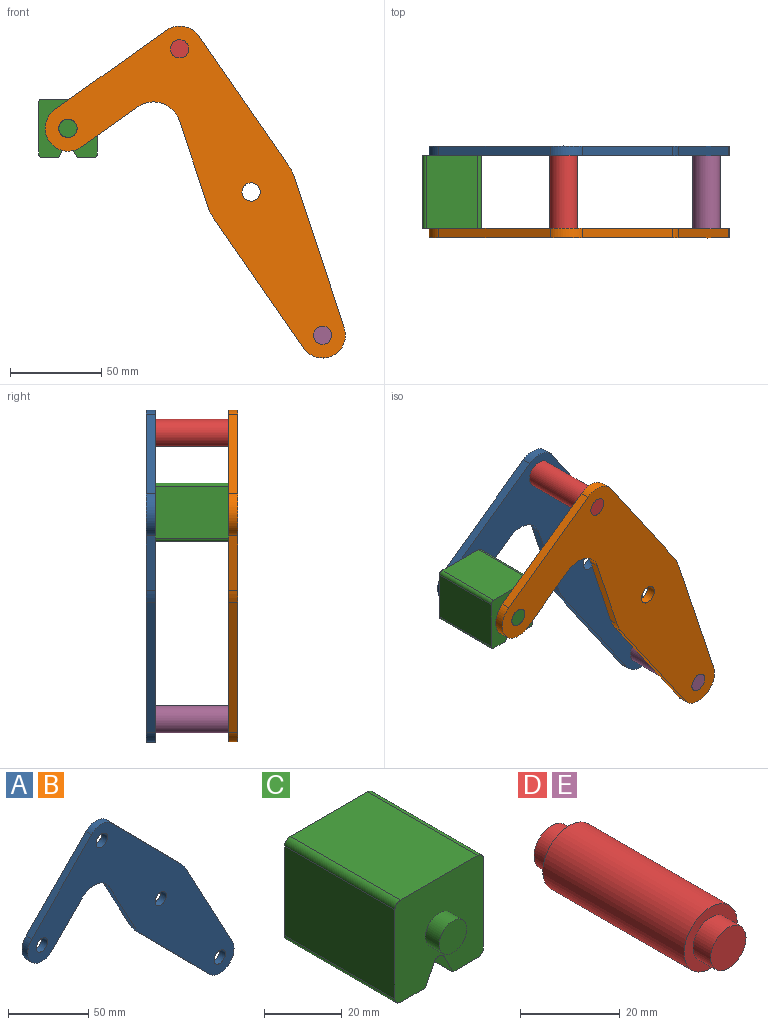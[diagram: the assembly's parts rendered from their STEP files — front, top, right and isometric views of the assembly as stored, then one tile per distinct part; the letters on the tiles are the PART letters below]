
ASSEMBLY  parts=5 mates=3
PART A: 18 faces, bbox 181.7x5x165.8 mm
  f0: plane 43.49x23.35mm, normal (-0.88,0,-0.47), area 246.8mm2, adj f1,f14,f16,f17
  f1: cylinder r=25mm len=5.75mm, axis (0,1,0), area 35.8mm2, adj f0,f2,f16,f17
  f2: plane 61.6x60.87mm, normal (-0.71,0,-0.7), area 433mm2, adj f1,f3,f16,f17
  f3: cylinder r=12.5mm len=21.39mm, axis (0,1,0), area 178.4mm2, adj f2,f4,f16,f17
  f4: plane 76.3x40.96mm, normal (0.88,0,0.47), area 433mm2, adj f3,f5,f16,f17
  f5: cylinder r=25mm len=5.75mm, axis (0,1,0), area 35.8mm2, adj f4,f6,f16,f17
  f6: plane 61.6x60.87mm, normal (0.71,0,0.7), area 433mm2, adj f5,f7,f16,f17
  f7: cylinder r=12.5mm len=17.78mm, axis (0,1,0), area 98.9mm2, adj f6,f8,f16,f17
  f8: plane 53.35x52.71mm, normal (-0.71,0,0.7), area 375mm2, adj f7,f9,f16,f17
  f9: cylinder r=12.5mm len=21.39mm, axis (0,1,0), area 196.3mm2, adj f8,f10,f16,f17
  f10: plane 26.86x26.54mm, normal (0.71,0,-0.7), area 188.8mm2, adj f9,f14,f16,f17
  f11: cylinder r=5mm len=10mm, axis (0,1,0), area 157.1mm2, adj f16,f17
  f12: cylinder r=5mm len=10mm, axis (0,1,0), area 157.1mm2, adj f16,f17
  f13: cylinder r=5mm len=10mm, axis (0,1,0), area 157.1mm2, adj f16,f17
  f14: cylinder r=15mm len=23.89mm, axis (0,1,0), area 140.2mm2, adj f0,f10,f16,f17
  f15: cylinder r=5mm len=10mm, axis (0,1,0), area 157.1mm2, adj f16,f17
  f16: plane 181.66x165.78mm, normal (0,-1,0), area 8710.1mm2, adj f0,f1,f2,f3,f4,f5,f6,f7
  f17: plane 181.66x165.78mm, normal (0,1,0), area 8710.1mm2, adj f0,f1,f2,f3,f4,f5,f6,f7
PART B: same geometry as A
PART C: 18 faces, bbox 32.1x50x32.1 mm
  f0: plane 40x28.08mm, normal (1,0,0), area 1123.1mm2, adj f4,f10,f13,f14
  f1: plane 40x9.04mm, normal (0,0,-1), area 361.6mm2, adj f2,f4,f10,f14
  f2: plane 40x6.42mm, normal (-0.89,0,-0.45), area 287.2mm2, adj f1,f4,f10,f15
  f3: plane 40x6.42mm, normal (0.89,0,-0.45), area 287.2mm2, adj f4,f5,f10,f15
  f4: plane 32.08x32.08mm, normal (0,-1,0), area 900.6mm2, adj f0,f1,f2,f3,f5,f6,f7,f9
  f5: plane 40x9.04mm, normal (0,0,-1), area 361.6mm2, adj f3,f4,f10,f16
  f6: plane 40x28.08mm, normal (0,0,1), area 1123.1mm2, adj f4,f10,f13,f17
  f7: plane 40x28.08mm, normal (-1,0,0), area 1123.1mm2, adj f4,f10,f16,f17
  f8: plane 10x10mm, normal (0,-1,0), area 78.5mm2, adj f9
  f9: cylinder r=5mm len=10mm, axis (0,1,0), area 157.1mm2, adj f4,f8
  f10: plane 32.08x32.08mm, normal (0,1,0), area 900.6mm2, adj f0,f1,f2,f3,f5,f6,f7,f12
  f11: plane 10x10mm, normal (0,1,0), area 78.5mm2, adj f12
  f12: cylinder r=5mm len=10mm, axis (0,-1,0), area 157.1mm2, adj f10,f11
  f13: cylinder r=2mm len=40mm, axis (0,1,0), area 125.7mm2, adj f0,f4,f6,f10
  f14: cylinder r=2mm len=40mm, axis (0,-1,0), area 125.7mm2, adj f0,f1,f4,f10
  f15: cylinder r=2mm len=40mm, axis (0,1,0), area 177.1mm2, adj f2,f3,f4,f10
  f16: cylinder r=2mm len=40mm, axis (0,1,0), area 125.7mm2, adj f4,f5,f7,f10
  f17: cylinder r=2mm len=40mm, axis (0,-1,0), area 125.7mm2, adj f4,f6,f7,f10
PART D: 7 faces, bbox 15x50x15 mm
  f0: cylinder r=7.5mm len=40mm, axis (0,-1,0), area 1885mm2, adj f2,f5
  f1: cylinder r=5mm len=10mm, axis (0,1,0), area 157.1mm2, adj f2,f3
  f2: plane 15x15mm, normal (0,-1,0), area 98.2mm2, adj f0,f1
  f3: plane 10x10mm, normal (0,-1,0), area 78.5mm2, adj f1
  f4: cylinder r=5mm len=10mm, axis (0,-1,0), area 157.1mm2, adj f5,f6
  f5: plane 15x15mm, normal (0,1,0), area 98.2mm2, adj f0,f4
  f6: plane 10x10mm, normal (0,1,0), area 78.5mm2, adj f4
PART E: same geometry as D
PLACE A rot(axis=(0,1,0),9.9deg) t=(0,25,0)mm
PLACE B rot(axis=(0,1,0),9.9deg) t=(0,-20,0)mm fixed
PLACE C t=(4.5,-20,17.78)mm
PLACE D rot(axis=(0,1,0),9.9deg) t=(0,-20,0)mm
PLACE E rot(axis=(0,1,0),9.9deg) t=(78.14,-20,-156.58)mm
MATE fastened A.f7 <-> D.f0  axis (0,-1,0) through (-39.07,20,78.29)mm
MATE revolute C.f9 <-> B.f9  axis (0,1,0) through (-100.19,-20,34.82)mm
MATE fastened E.f0 <-> B.f3  axis (0,1,0) through (39.07,-20,-78.29)mm
